# Revit family: Plymold-Receptacles-Economy_Waste
name_source: partatom
category: Furniture
units: mm (PartAtom-declared; Revit-internal decimal feet)

## family parameters
Always vertical = Yes
Cut with Voids When Loaded = No
OmniClass Number = 23.40.20.00
OmniClass Title = General Furniture and Specialties
Render Appearance Source = Family Geometry
Room Calculation Point = No
Shared = No
Work Plane-Based = No

## types (1)
- 80501
    Assembly Code = E2020200
    BACK MATERIAL = PLY - Wood Mahogany - Vertical
    BASE MATERIAL = PLY - Onyx Black Powdercoat
    DOOR MATERIAL = PLY - Wood Mahogany - Vertical
    Default Elevation = 0"
    Depth = 23"
    Description = Shelf Top Waste Receptacle - 23"W x 23"D x 41.5"H
    EDGE MATERIAL = PLY - Wood Mahogany - Vertical
    GLIDES MATERIAL = PLY - Plastic Black
    Height = 42 1/2"
    Keynote = 12500
    Manufacturer = Plymold Inc.
    Model = 80501
    Product Documentation Link = https://plymold.com
    Revit File Built By = https://servex-us.com
    SIDE MATERIAL = PLY - Wood Mahogany - Vertical
    Sustainability = https://plymold.com
    TOP MATERIAL = PLY - Wood Mahogany - Horizontal
    Type Comments = Receptacles
    URL = https://plymold.com
    Width = 23"

## geometry (parser evidence)
native form markers: Sweep x2
no freeform markers — native parametric forms only
